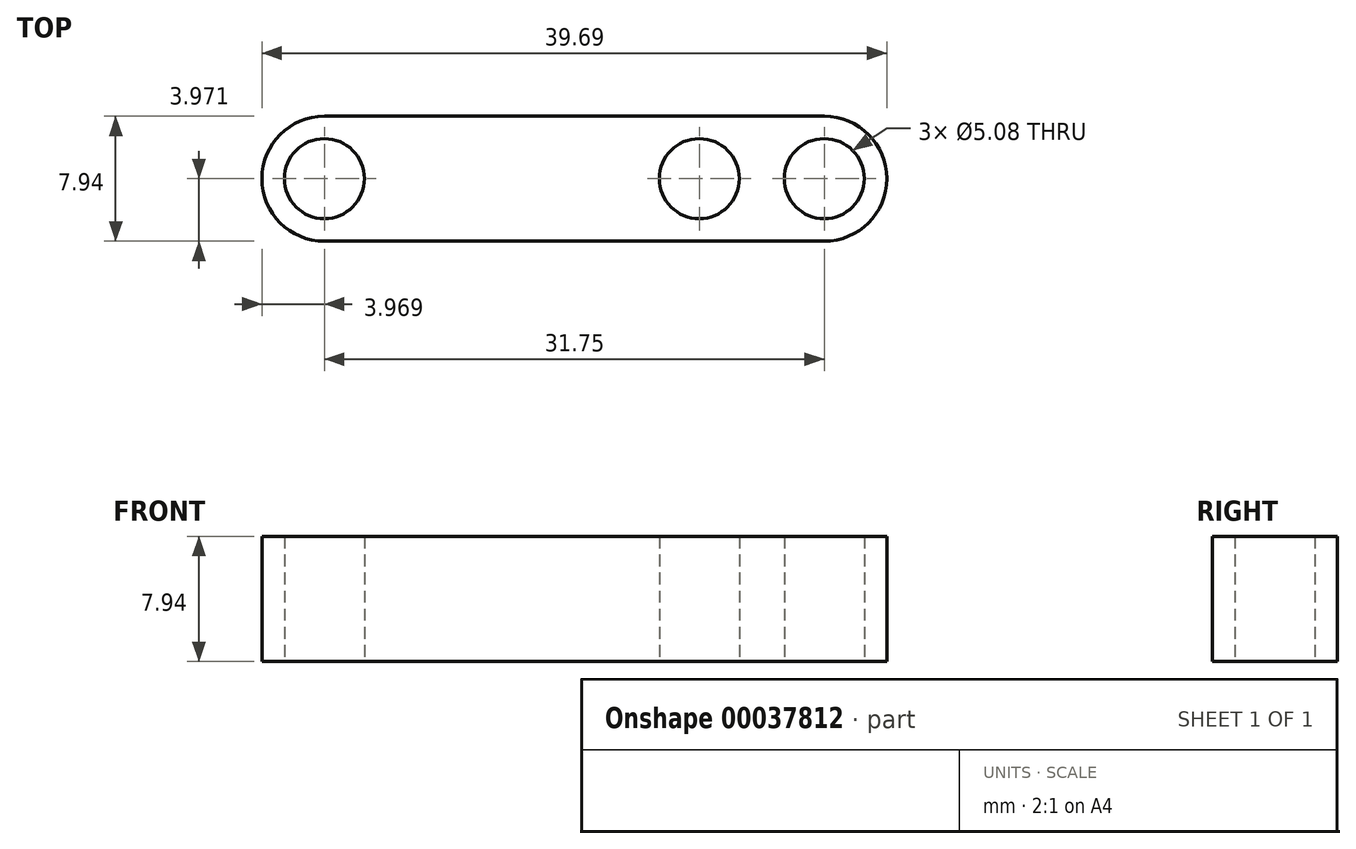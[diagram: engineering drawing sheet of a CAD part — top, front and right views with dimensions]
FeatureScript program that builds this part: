
annotation { "Feature Type Name" : "Feature", "Feature Type Description" : "" }
export const myFeature = defineFeature(function(context is Context, id is Id, definition is map)
    precondition{}
    {
        {
            var Q0;
            Q0=qCreatedBy(makeId("Top.planeOp"),FACE);
            var sketch = newSketch(context, id + "F0", { "sketchPlane" : qUnion([Q0])});
            skLineSegment(sketch, "E0.bottom", {"start": v(0, 0) * mm, "end": v(39.69, 0) * mm});
            skLineSegment(sketch, "E0.top", {"start": v(0, -7.94) * mm, "end": v(39.69, -7.94) * mm});
            skLineSegment(sketch, "E0.left", {"start": v(0, 0) * mm, "end": v(0, -7.94) * mm});
            skLineSegment(sketch, "E0.right", {"start": v(39.69, 0) * mm, "end": v(39.69, -7.94) * mm});
            skLineSegment(sketch, "E1", {"start": v(0, -3.97) * mm, "end": v(3.97, -3.97) * mm, "construction": true});
            skLineSegment(sketch, "E2", {"start": v(35.72, -3.97) * mm, "end": v(39.69, -3.97) * mm, "construction": true});
            skCircle(sketch, "E3", {"center": v(3.97, -3.97) * mm, "radius": 2.54 * mm});
            skCircle(sketch, "E4", {"center": v(35.72, -3.97) * mm, "radius": 2.54 * mm});
            skLineSegment(sketch, "E5", {"start": v(35.72, -3.97) * mm, "end": v(27.78, -3.97) * mm, "construction": true});
            skCircle(sketch, "E6", {"center": v(27.78, -3.97) * mm, "radius": 2.54 * mm});
            skSolve(sketch);
        }
        {
            var Q0;
            Q0=qSketchRegion(id+"F0",true);
            extrude(context, id + "F1", {"entities" : qUnion([Q0]), "depth" : 7.94 * mm});
        }
        {
            var Q0;
            Q0=makeQuery(id+"F1.opExtrude","SWEPT_EDGE",EDGE,{"disambiguationData":[OSD([sQuery(id+"F0.wireOp",EDGE,"E0.bottom"),sQuery(id+"F0.wireOp",EDGE,"E0.left")])]});
            var Q1;
            Q1=makeQuery(id+"F1.opExtrude","SWEPT_EDGE",EDGE,{"disambiguationData":[OSD([sQuery(id+"F0.wireOp",EDGE,"E0.top"),sQuery(id+"F0.wireOp",EDGE,"E0.left")])]});
            var Q2;
            Q2=makeQuery(id+"F1.opExtrude","SWEPT_EDGE",EDGE,{"disambiguationData":[OSD([sQuery(id+"F0.wireOp",EDGE,"E0.top"),sQuery(id+"F0.wireOp",EDGE,"E0.right")])]});
            var Q3;
            Q3=makeQuery(id+"F1.opExtrude","SWEPT_EDGE",EDGE,{"disambiguationData":[OSD([sQuery(id+"F0.wireOp",EDGE,"E0.bottom"),sQuery(id+"F0.wireOp",EDGE,"E0.right")])]});
            fillet(context, id + "F2", {"entities" : qUnion([Q0, Q1, Q2, Q3]), "radius" : 3.97 * mm, "tangentPropagation" : true, "allowEdgeOverflow" : false});
        }
    });
